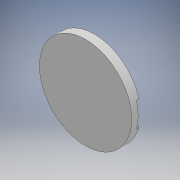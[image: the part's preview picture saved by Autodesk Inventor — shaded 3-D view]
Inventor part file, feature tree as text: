
AUTODESK INVENTOR PART (.ipt)
format: ipt  version: 2018 (Build 220112000, 112)  size: 194,048 bytes
history: native  units: mm
features: extrude x5, sketch x5, fillet x1, pattern_circular x1
ambient origin geometry x8: Origin, YZ Plane, XZ Plane, XY Plane, X Axis, Y Axis, Z Axis, Center Point
bodies: Solid1 (feature_tree)
feature tree (12):
  extrude  "Extrusion1"  Depth=0.4mm
  extrude  "Extrusion2"  Depth=5.0mm
  extrude  "Extrusion3"  Depth=27.25mm
  fillet  "Fillet1"  Radius=22.514747mm
  pattern_circular  "Circular Pattern1"  [2 undecoded]
  extrude  "Extrusion4"  Depth=1.5mm
  extrude  "Extrusion7"  Depth=1.5mm TaperAngle=0.0deg
  sketch  "Sketch1"  dims[d2=0.4mm d3=0.0mm d4=54.5mm]
  sketch  "Sketch2"  dims[d5=5.0mm d6=0.0mm d7=56.0mm]
  sketch  "Sketch3"  dims[d8=56.0mm d9=27.25mm d10=22.514747mm]
  sketch  "Sketch4"  dims[d11=0.698132mm]
  sketch  "Sketch7"  dims[d12=26.25mm d13=22.514747mm d14=0.698132mm d15=1.4mm d16=0.0mm d17=0.5mm d18=20.0mm d19=360.0deg d25=7.5mm d26=3.0mm d27=7.5mm d28=3.0mm d29=1.5mm d30=0.0mm d47=48.0mm d48=1.5mm d49=0.0mm d50=54.5mm d51=3.0mm d52=7.5mm d53=3.0mm d54=7.5mm]
note: 2 required parameter values undecoded (feature->parameter linkage not recoverable at this tier; creation-order binding heuristic only, values carry confidence <= 0.55)
